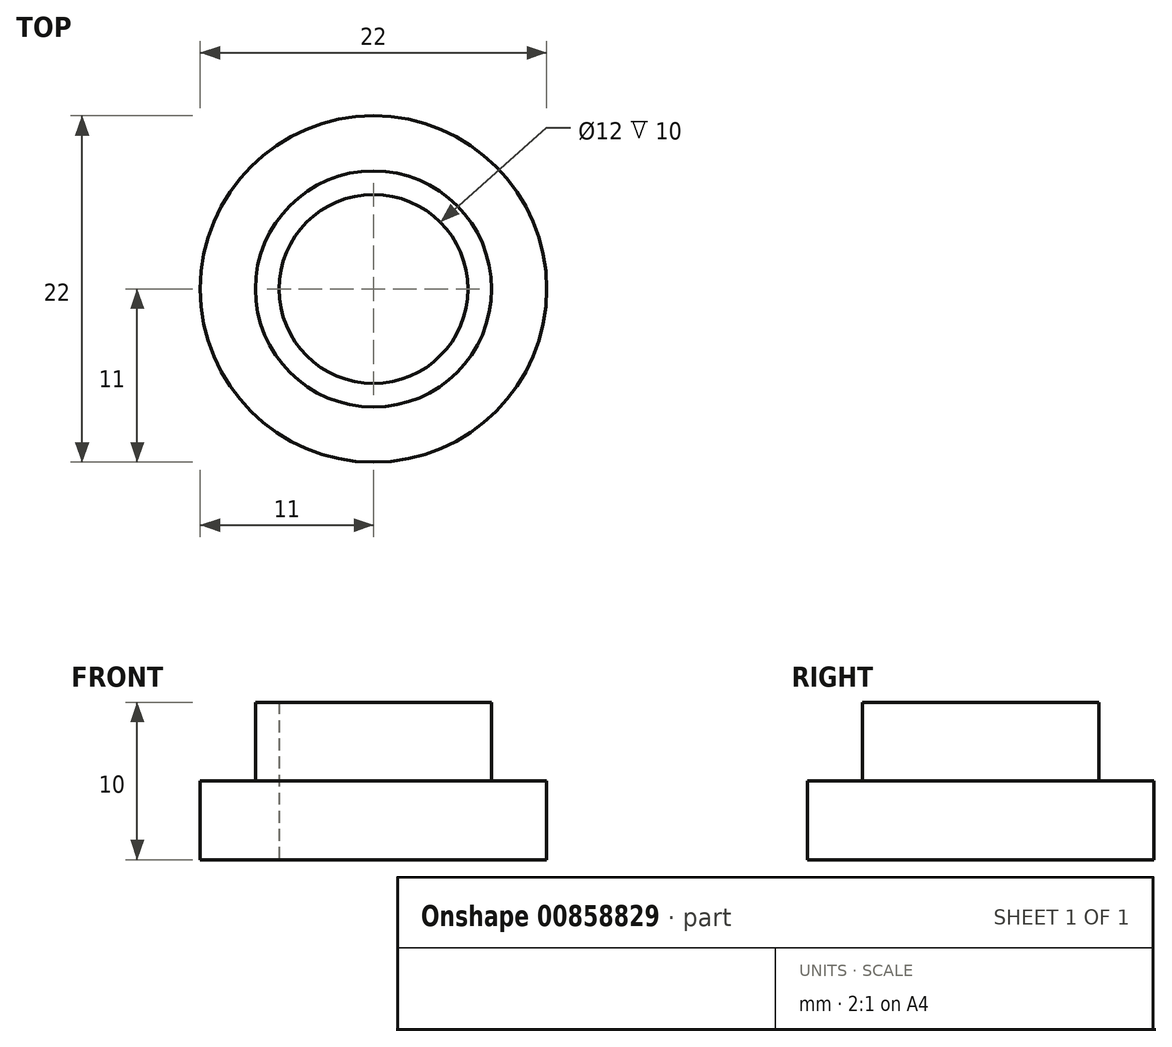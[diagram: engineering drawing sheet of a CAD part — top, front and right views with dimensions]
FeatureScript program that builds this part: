
annotation { "Feature Type Name" : "Feature", "Feature Type Description" : "" }
export const myFeature = defineFeature(function(context is Context, id is Id, definition is map)
    precondition{}
    {
        {
            var Q0;
            Q0=qCreatedBy(makeId("Front.planeOp"),FACE);
            var sketch = newSketch(context, id + "F0", { "sketchPlane" : qUnion([Q0])});
            skLineSegment(sketch, "E0", {"start": v(0, 0) * mm, "end": v(0, 18.98) * mm, "construction": true});
            skLineSegment(sketch, "E1", {"start": v(0, 0) * mm, "end": v(-6, 0) * mm, "construction": true});
            skLineSegment(sketch, "E2", {"start": v(-6, 0) * mm, "end": v(-6, 10) * mm});
            skLineSegment(sketch, "E3", {"start": v(-6, 0) * mm, "end": v(-11, 0) * mm});
            skLineSegment(sketch, "E4", {"start": v(-11, 0) * mm, "end": v(-11, 5) * mm});
            skLineSegment(sketch, "E5", {"start": v(-6, 10) * mm, "end": v(-7.5, 10) * mm});
            skLineSegment(sketch, "E6", {"start": v(-7.5, 10) * mm, "end": v(-7.5, 5) * mm});
            skLineSegment(sketch, "E7", {"start": v(-7.5, 5) * mm, "end": v(-11, 5) * mm});
            skSolve(sketch);
        }
        {
            var Q0;
            Q0=makeQuery(id+"F0.imprint","IMPRINT",FACE,{"disambiguationData":[TD([[makeQuery(id+"F0.imprint","IMPRINT",EDGE,{"derivedFrom":sQuery(id+"F0.wireOp",EDGE,"E2")}),1.0]])]});
            var Q1;
            Q1=sQuery(id+"F0.wireOp",EDGE,"E0");
            revolve(context, id + "F1", {"surfaceOperationType" : NewSurfaceOperationType.NEW, "entities" : qUnion([Q0]), "axis" : qUnion([Q1]), "revolveType" : RevolveType.FULL});
        }
    });
